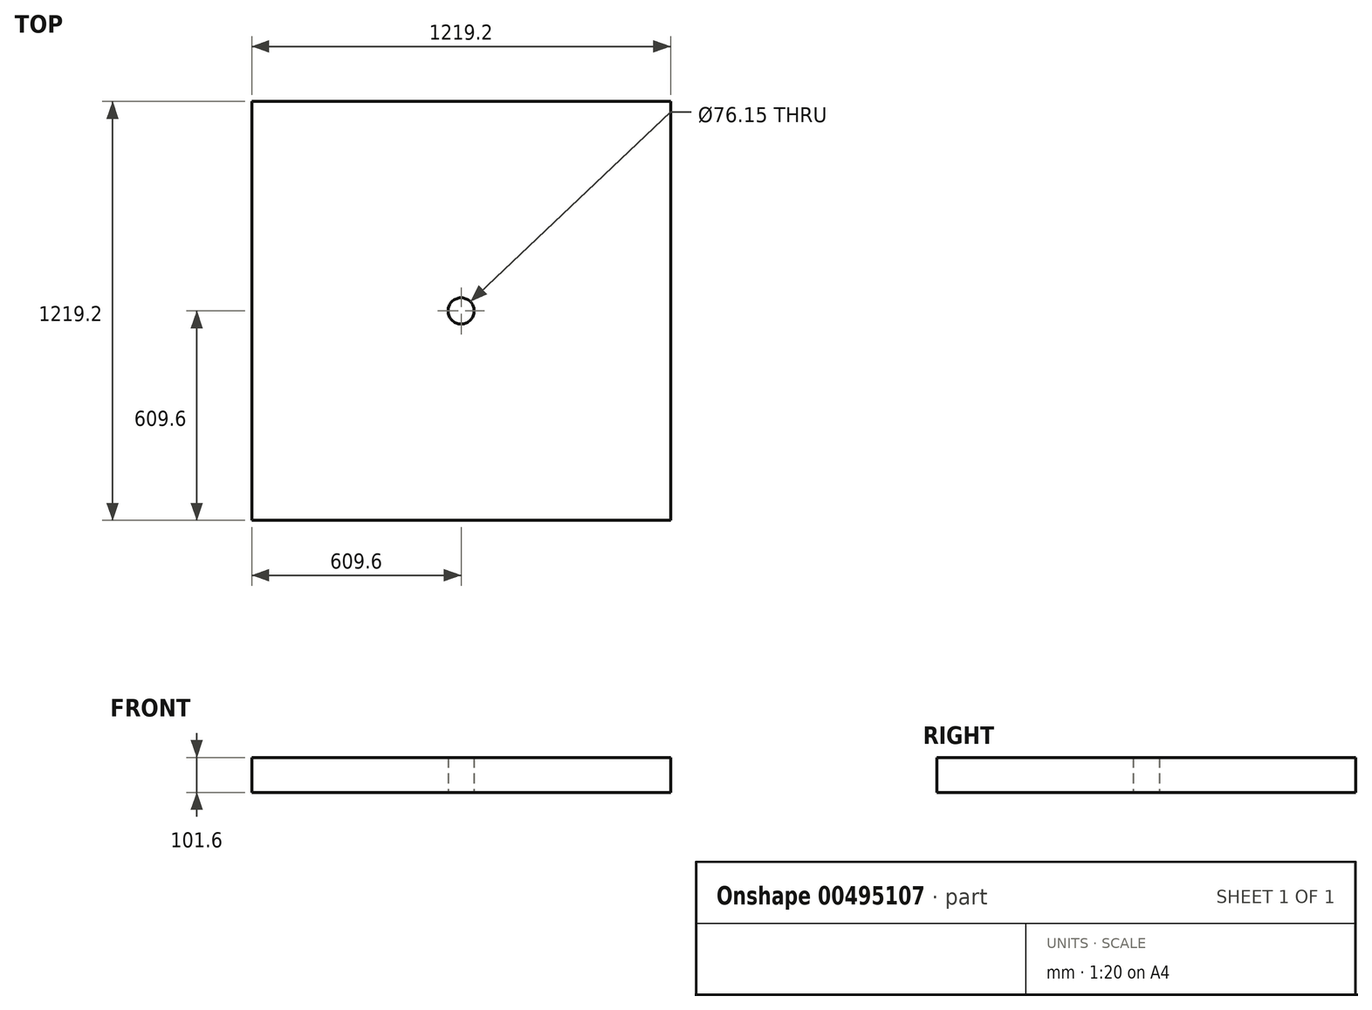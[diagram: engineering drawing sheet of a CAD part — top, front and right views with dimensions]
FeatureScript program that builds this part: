
annotation { "Feature Type Name" : "Feature", "Feature Type Description" : "" }
export const myFeature = defineFeature(function(context is Context, id is Id, definition is map)
    precondition{}
    {
        {
            var Q0;
            Q0=qCreatedBy(makeId("Top.planeOp"),FACE);
            var sketch = newSketch(context, id + "F0", { "sketchPlane" : qUnion([Q0])});
            skLineSegment(sketch, "E0", {"start": v(609.6, 609.6) * mm, "end": v(-609.6, 609.6) * mm});
            skLineSegment(sketch, "E1", {"start": v(-609.6, 609.6) * mm, "end": v(-609.6, -609.6) * mm});
            skLineSegment(sketch, "E2", {"start": v(-609.6, -609.6) * mm, "end": v(609.6, -609.6) * mm});
            skLineSegment(sketch, "E3", {"start": v(609.6, -609.6) * mm, "end": v(609.6, 609.6) * mm});
            skPoint(sketch, "E4.centerSnap0", {"position": v(0, 609.6) * mm});
            skPoint(sketch, "E5", {"position": v(609.6, 0) * mm});
            skCircle(sketch, "E6", {"center": v(0, 0) * mm, "radius": 38.07 * mm});
            skCircle(sketch, "E7", {"center": v(0, 0) * mm, "radius": 36.54 * mm});
            skSolve(sketch);
        }
        {
            var Q0;
            Q0=makeQuery(id+"F0.imprint","IMPRINT",FACE,{"disambiguationData":[TD([[makeQuery(id+"F0.imprint","IMPRINT",EDGE,{"derivedFrom":sQuery(id+"F0.wireOp",EDGE,"E0")}),1.0]])]});
            extrude(context, id + "F1", {"entities" : qUnion([Q0]), "depth" : 101.6 * mm});
        }
    });
